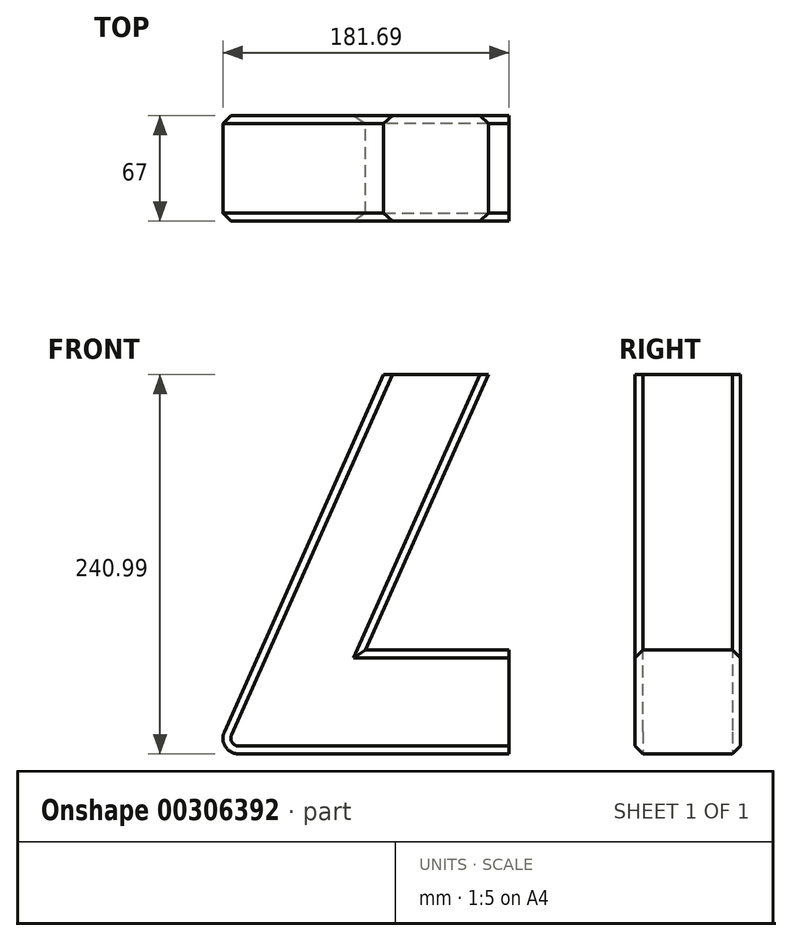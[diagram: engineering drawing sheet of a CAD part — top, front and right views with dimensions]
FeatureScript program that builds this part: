
annotation { "Feature Type Name" : "Feature", "Feature Type Description" : "" }
export const myFeature = defineFeature(function(context is Context, id is Id, definition is map)
    precondition{}
    {
        {
            var Q0;
            Q0=qCreatedBy(makeId("Front.planeOp"),FACE);
            var sketch = newSketch(context, id + "F0", { "sketchPlane" : qUnion([Q0])});
            skLineSegment(sketch, "E0", {"start": v(0, 66) * mm, "end": v(0, 0) * mm});
            skLineSegment(sketch, "E1.MirrorCS", {"start": v(-91, 66) * mm, "end": v(0, 66) * mm});
            skLineSegment(sketch, "E2.MirrorCS", {"start": v(-12.96, 240.99) * mm, "end": v(-91, 66) * mm});
            skLineSegment(sketch, "E3.MirrorCS", {"start": v(-79.62, 240.99) * mm, "end": v(-12.96, 240.99) * mm});
            skLineSegment(sketch, "E4.MirrorCS", {"start": v(-187.1, 0) * mm, "end": v(-79.62, 240.99) * mm});
            skLineSegment(sketch, "E5.MirrorCS", {"start": v(0, 0) * mm, "end": v(-187.1, 0) * mm});
            skSolve(sketch);
        }
        {
            var Q0;
            Q0=makeQuery(id+"F0.imprint","IMPRINT",FACE,{"disambiguationData":[TD([[makeQuery(id+"F0.imprint","IMPRINT",EDGE,{"derivedFrom":sQuery(id+"F0.wireOp",EDGE,"E1.MirrorCS")}),-1.0]])]});
            extrude(context, id + "F1", {"entities" : qUnion([Q0]), "depth" : 67 * mm});
        }
        {
            var Q0;
            Q0=makeQuery(id+"F1.opExtrude","SWEPT_EDGE",EDGE,{"disambiguationData":[OSD([sQuery(id+"F0.wireOp",EDGE,"E4.MirrorCS"),sQuery(id+"F0.wireOp",EDGE,"E5.MirrorCS")])]});
            fillet(context, id + "F2", {"entities" : qUnion([Q0]), "radius" : 10 * mm, "tangentPropagation" : true, "allowEdgeOverflow" : false});
        }
        {
            var Q0;
            Q0=makeQuery(id+"F1.opExtrude","CAP_EDGE",EDGE,{"disambiguationData":[OSD([sQuery(id+"F0.wireOp",EDGE,"E2.MirrorCS")])],"isStart":false});
            var Q1;
            Q1=makeQuery(id+"F1.opExtrude","CAP_EDGE",EDGE,{"disambiguationData":[OSD([sQuery(id+"F0.wireOp",EDGE,"E2.MirrorCS")])],"isStart":true});
            var Q2;
            Q2=makeQuery(id+"F1.opExtrude","CAP_EDGE",EDGE,{"disambiguationData":[OSD([sQuery(id+"F0.wireOp",EDGE,"E4.MirrorCS")])],"isStart":true});
            var Q3;
            Q3=makeQuery(id+"F1.opExtrude","CAP_EDGE",EDGE,{"disambiguationData":[OSD([sQuery(id+"F0.wireOp",EDGE,"E4.MirrorCS")])],"isStart":false});
            var Q4;
            Q4=makeQuery(id+"F1.opExtrude","CAP_EDGE",EDGE,{"disambiguationData":[OSD([sQuery(id+"F0.wireOp",EDGE,"E1.MirrorCS")])],"isStart":true});
            var Q5;
            Q5=makeQuery(id+"F1.opExtrude","CAP_EDGE",EDGE,{"disambiguationData":[OSD([sQuery(id+"F0.wireOp",EDGE,"E1.MirrorCS")])],"isStart":false});
            chamfer(context, id + "F3", {"entities" : qUnion([Q0, Q1, Q2, Q3, Q4, Q5]), "width" : 5 * mm, "tangentPropagation" : true});
        }
    });
